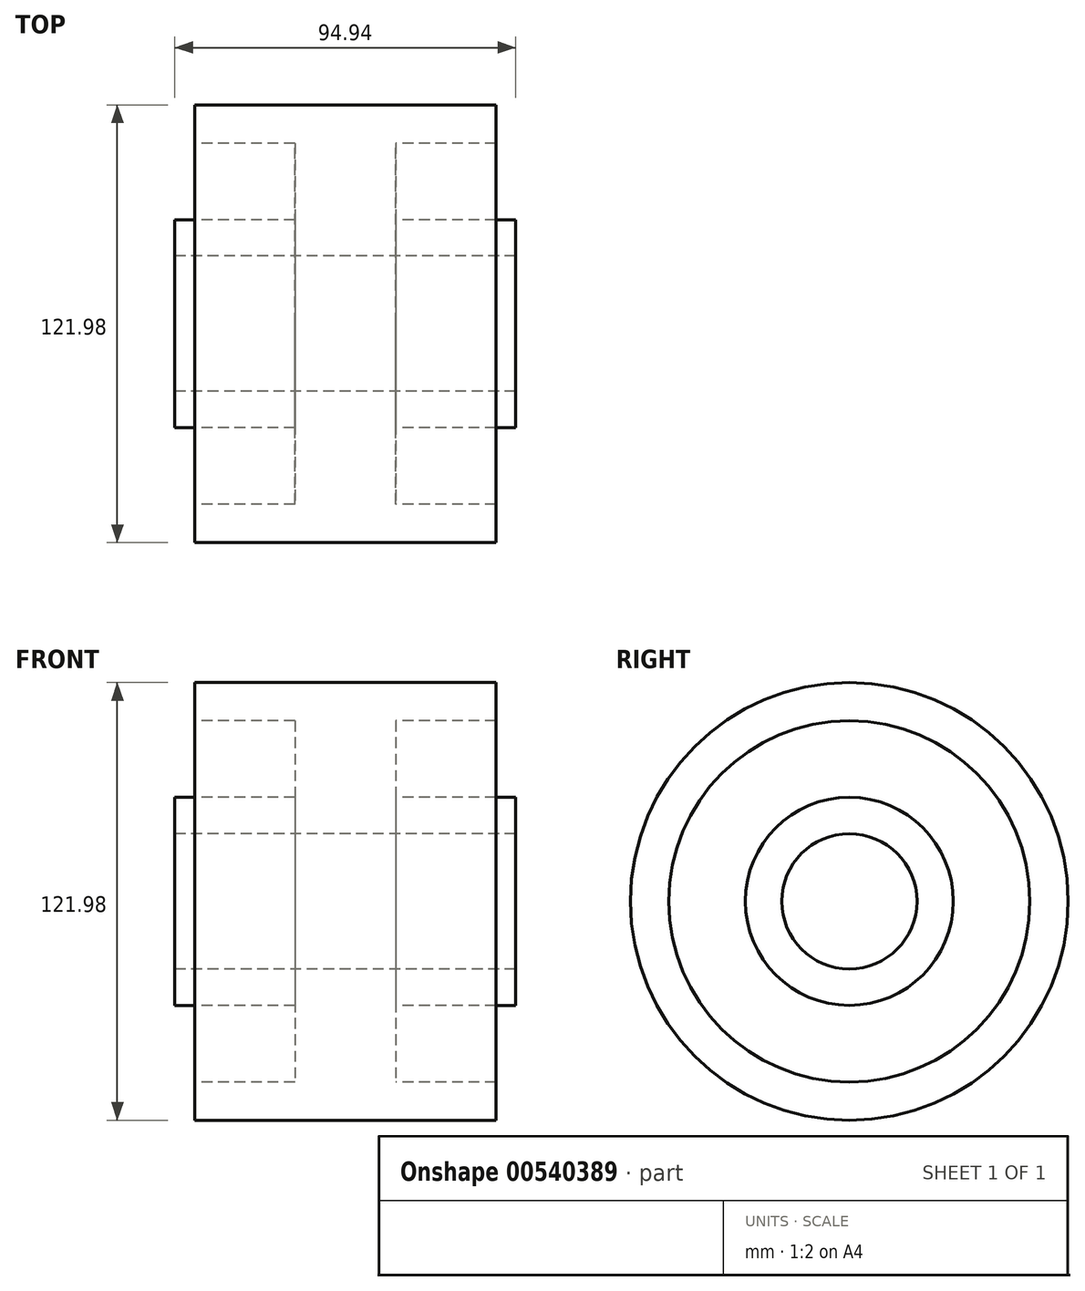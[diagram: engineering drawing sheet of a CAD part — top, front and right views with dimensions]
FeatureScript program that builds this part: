
annotation { "Feature Type Name" : "Feature", "Feature Type Description" : "" }
export const myFeature = defineFeature(function(context is Context, id is Id, definition is map)
    precondition{}
    {
        {
            var Q0;
            Q0=qCreatedBy(makeId("Front.planeOp"),FACE);
            var sketch = newSketch(context, id + "F0", { "sketchPlane" : qUnion([Q0])});
            skLineSegment(sketch, "E0", {"start": v(-88.01, 0) * mm, "end": v(65.07, 0) * mm, "construction": true});
            skLineSegment(sketch, "E1", {"start": v(0, 0) * mm, "end": v(0, 76.8) * mm, "construction": true});
            skLineSegment(sketch, "E2", {"start": v(0, 18.85) * mm, "end": v(-47.47, 18.85) * mm});
            skLineSegment(sketch, "E3", {"start": v(-47.47, 18.85) * mm, "end": v(-47.47, 28.98) * mm});
            skLineSegment(sketch, "E4", {"start": v(-47.47, 28.98) * mm, "end": v(-14.05, 28.98) * mm});
            skLineSegment(sketch, "E5", {"start": v(-14.05, 28.98) * mm, "end": v(-14.05, 50.32) * mm});
            skLineSegment(sketch, "E6", {"start": v(-14.05, 50.32) * mm, "end": v(-41.96, 50.32) * mm});
            skLineSegment(sketch, "E7", {"start": v(-41.96, 50.32) * mm, "end": v(-41.96, 60.99) * mm});
            skLineSegment(sketch, "E8", {"start": v(-41.96, 60.99) * mm, "end": v(0, 60.99) * mm});
            skLineSegment(sketch, "E9.MirrorCS", {"start": v(47.47, 28.98) * mm, "end": v(14.05, 28.98) * mm});
            skLineSegment(sketch, "E10.MirrorCS", {"start": v(14.05, 28.98) * mm, "end": v(14.05, 50.32) * mm});
            skLineSegment(sketch, "E11.MirrorCS", {"start": v(14.05, 50.32) * mm, "end": v(41.96, 50.32) * mm});
            skLineSegment(sketch, "E12.MirrorCS", {"start": v(47.47, 18.85) * mm, "end": v(47.47, 28.98) * mm});
            skLineSegment(sketch, "E13.MirrorCS", {"start": v(41.96, 60.99) * mm, "end": v(0, 60.99) * mm});
            skLineSegment(sketch, "E14.MirrorCS", {"start": v(41.96, 50.32) * mm, "end": v(41.96, 60.99) * mm});
            skLineSegment(sketch, "E15.MirrorCS", {"start": v(0, 18.85) * mm, "end": v(47.47, 18.85) * mm});
            skSolve(sketch);
        }
        {
            var Q0;
            Q0 = qSketchRegion(id + "F0", true);
            var Q1;
            Q1=sQuery(id+"F0.wireOp",EDGE,"E0");
            revolve(context, id + "F1", {"entities" : qUnion([Q0]), "axis" : qUnion([Q1]), "revolveType" : RevolveType.FULL});
        }
    });
